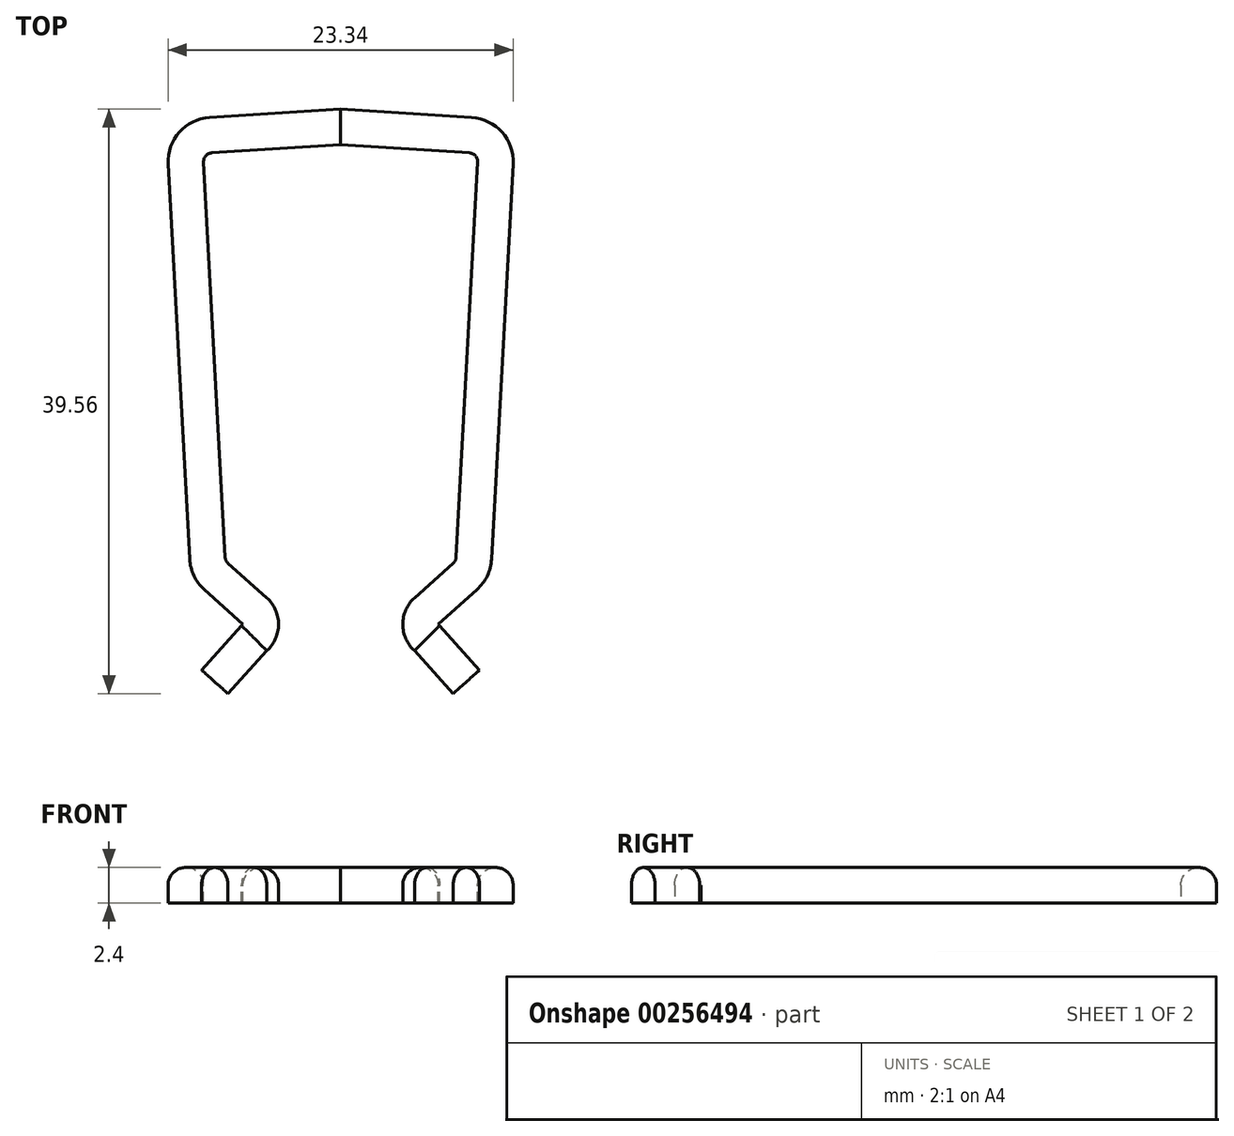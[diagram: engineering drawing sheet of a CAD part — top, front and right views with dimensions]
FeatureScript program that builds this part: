
annotation { "Feature Type Name" : "Feature", "Feature Type Description" : "" }
export const myFeature = defineFeature(function(context is Context, id is Id, definition is map)
    precondition{}
    {
        {
            var Q0;
            Q0=qCreatedBy(makeId("Top.planeOp"),FACE);
            var sketch = newSketch(context, id + "F0", { "sketchPlane" : qUnion([Q0]), "disableImprinting" : false});
            skLineSegment(sketch, "E0", {"start": v(-2.6, -9.39) * mm, "end": v(2.6, -9.39) * mm, "construction": true});
            skPoint(sketch, "E1", {"position": v(0, -9.39) * mm});
            skLineSegment(sketch, "E2", {"start": v(2.6, -9.3) * mm, "end": v(3.09, -0.4) * mm});
            skLineSegment(sketch, "E3", {"start": v(2.9, -0.19) * mm, "end": v(0, 0) * mm});
            skLineSegment(sketch, "E4", {"start": v(0, 0) * mm, "end": v(-2.9, -0.19) * mm});
            skLineSegment(sketch, "E5", {"start": v(-3.09, -0.4) * mm, "end": v(-2.6, -9.3) * mm});
            skLineSegment(sketch, "E6", {"start": v(-3.1, -0.2) * mm, "end": v(3.1, -0.2) * mm, "construction": true});
            skPoint(sketch, "E7", {"position": v(0, -0.2) * mm});
            skLineSegment(sketch, "E8", {"start": v(2.54, -9.44) * mm, "end": v(1.67, -10.22) * mm});
            skArc(sketch, "E9", {"start": v(1.67, -10.22) * mm, "mid": v(1.4, -10.82) * mm, "end": v(1.67, -11.42) * mm});
            skLineSegment(sketch, "E10", {"start": v(1.67, -11.42) * mm, "end": v(2.54, -12.39) * mm});
            skLineSegment(sketch, "E11", {"start": v(0, -10.7) * mm, "end": v(2.2, -10.82) * mm, "construction": true});
            skLineSegment(sketch, "E12.MirrorCS", {"start": v(-1.67, -11.42) * mm, "end": v(-2.54, -12.39) * mm});
            skArc(sketch, "E13.MirrorCS", {"start": v(-1.67, -10.22) * mm, "mid": v(-1.4, -10.82) * mm, "end": v(-1.67, -11.42) * mm});
            skLineSegment(sketch, "E14.MirrorCS", {"start": v(0, -10.7) * mm, "end": v(-2.2, -10.82) * mm, "construction": true});
            skLineSegment(sketch, "E15.MirrorCS", {"start": v(-2.54, -9.44) * mm, "end": v(-1.67, -10.22) * mm});
            skPoint(sketch, "E16.visualSharp", {"position": v(2.6, -9.39) * mm});
            skArc(sketch, "E16.filletArc", {"start": v(2.54, -9.44) * mm, "mid": v(2.59, -9.38) * mm, "end": v(2.6, -9.3) * mm});
            skPoint(sketch, "E17.visualSharp", {"position": v(3.1, -0.2) * mm});
            skArc(sketch, "E17.filletArc", {"start": v(3.09, -0.4) * mm, "mid": v(3.04, -0.25) * mm, "end": v(2.9, -0.19) * mm});
            skPoint(sketch, "E18.visualSharp", {"position": v(-3.1, -0.2) * mm});
            skArc(sketch, "E18.filletArc", {"start": v(-2.9, -0.19) * mm, "mid": v(-3.04, -0.25) * mm, "end": v(-3.09, -0.4) * mm});
            skPoint(sketch, "E19.visualSharp", {"position": v(-2.6, -9.39) * mm});
            skArc(sketch, "E19.filletArc", {"start": v(-2.6, -9.3) * mm, "mid": v(-2.59, -9.38) * mm, "end": v(-2.54, -9.44) * mm});
            skSolve(sketch);
        }
        {
            var Q0;
            Q0=sQuery(id+"F0.wireOp",EDGE,"E10");
            var Q1;
            Q1=sQuery(id+"F0.wireOp",VERTEX,"E10.end");
            cPlane(context, id + "F1", {"entities" : qUnion([Q0, Q1]), "cplaneType" : CPlaneType.CURVE_POINT, "offset" : 12.18 * mm, "width" : 150 * mm, "height" : 150 * mm});
        }
        {
            var Q0;
            Q0=qCreatedBy(id+"F1.planeOp",FACE);
            var sketch = newSketch(context, id + "F2", { "sketchPlane" : qUnion([Q0])});
            skCircle(sketch, "E20", {"center": v(-5.98, 0) * mm, "radius": 0.4 * mm});
            skLineSegment(sketch, "E21", {"start": v(-6.38, 0) * mm, "end": v(-6.38, -0.4) * mm});
            skLineSegment(sketch, "E22", {"start": v(-6.38, -0.4) * mm, "end": v(-5.98, -0.4) * mm});
            skLineSegment(sketch, "E23", {"start": v(-5.98, -0.4) * mm, "end": v(-5.58, -0.4) * mm});
            skLineSegment(sketch, "E24", {"start": v(-5.58, -0.4) * mm, "end": v(-5.58, 0) * mm});
            skSolve(sketch);
        }
        {
            var Q0;
            Q0=makeQuery(id+"F2.imprint","IMPRINT",FACE,{"disambiguationData":[TD([[makeQuery(id+"F2.imprint","IMPRINT",EDGE,{"derivedFrom":sQuery(id+"F2.wireOp",EDGE,"E20")}),1.0]])]});
            var Q1;
            {var subQ0=sQuery(id+"F2.wireOp",EDGE,"E21");Q1=makeQuery(id+"F2.imprint","IMPRINT",FACE,{"disambiguationData":[TD([[makeQuery(id+"F2.imprint","IMPRINT",EDGE,{"derivedFrom":subQ0}),1.0]])]});}
            var Q2;
            {var subQ0=sQuery(id+"F2.wireOp",EDGE,"E23");Q2=makeQuery(id+"F2.imprint","IMPRINT",FACE,{"disambiguationData":[TD([[makeQuery(id+"F2.imprint","IMPRINT",EDGE,{"derivedFrom":subQ0}),1.0]])]});}
            var Q3;
            Q3=sQuery(id+"F0.wireOp",EDGE,"E10");
            var Q4;
            Q4=sQuery(id+"F0.wireOp",EDGE,"E9");
            var Q5;
            Q5=sQuery(id+"F0.wireOp",EDGE,"E8");
            var Q6;
            Q6=sQuery(id+"F0.wireOp",EDGE,"E16.filletArc");
            var Q7;
            Q7=sQuery(id+"F0.wireOp",EDGE,"E2");
            var Q8;
            Q8=sQuery(id+"F0.wireOp",EDGE,"E17.filletArc");
            var Q9;
            Q9=sQuery(id+"F0.wireOp",EDGE,"E3");
            var Q10;
            Q10=sQuery(id+"F0.wireOp",EDGE,"E4");
            var Q11;
            Q11=sQuery(id+"F0.wireOp",EDGE,"E18.filletArc");
            var Q12;
            Q12=sQuery(id+"F0.wireOp",EDGE,"E5");
            var Q13;
            Q13=sQuery(id+"F0.wireOp",EDGE,"E19.filletArc");
            var Q14;
            Q14=sQuery(id+"F0.wireOp",EDGE,"E15.MirrorCS");
            var Q15;
            Q15=sQuery(id+"F0.wireOp",EDGE,"E13.MirrorCS");
            var Q16;
            Q16=sQuery(id+"F0.wireOp",EDGE,"E12.MirrorCS");
            sweep(context, id + "F3", {"profiles" : qUnion([Q0, Q1, Q2]), "path" : qUnion([Q3, Q4, Q5, Q6, Q7, Q8, Q9, Q10, Q11, Q12, Q13, Q14, Q15, Q16])});
        }
        {
            var Q0;
            Q0=makeQuery(id+"F3.opSweep","SWEPT_BODY",BODY,{"disambiguationData":[OSD([sQuery(id+"F0.wireOp",EDGE,"E12.MirrorCS"),sQuery(id+"F2.wireOp",EDGE,"E20"),sQuery(id+"F2.wireOp",EDGE,"E21"),sQuery(id+"F2.wireOp",EDGE,"E22"),sQuery(id+"F2.wireOp",EDGE,"E23"),sQuery(id+"F2.wireOp",EDGE,"E24")])]});
            var Q1;
            Q1=qCreatedBy(makeId("Origin.pointOp"),VERTEX);
            transform(context, id + "F4", {"entities" : qUnion([Q0]), "transformType" : TransformType.SCALE_UNIFORMLY, "scale" : 3, "scalePoint" : qUnion([Q1]), "makeCopy" : false});
        }
    });
